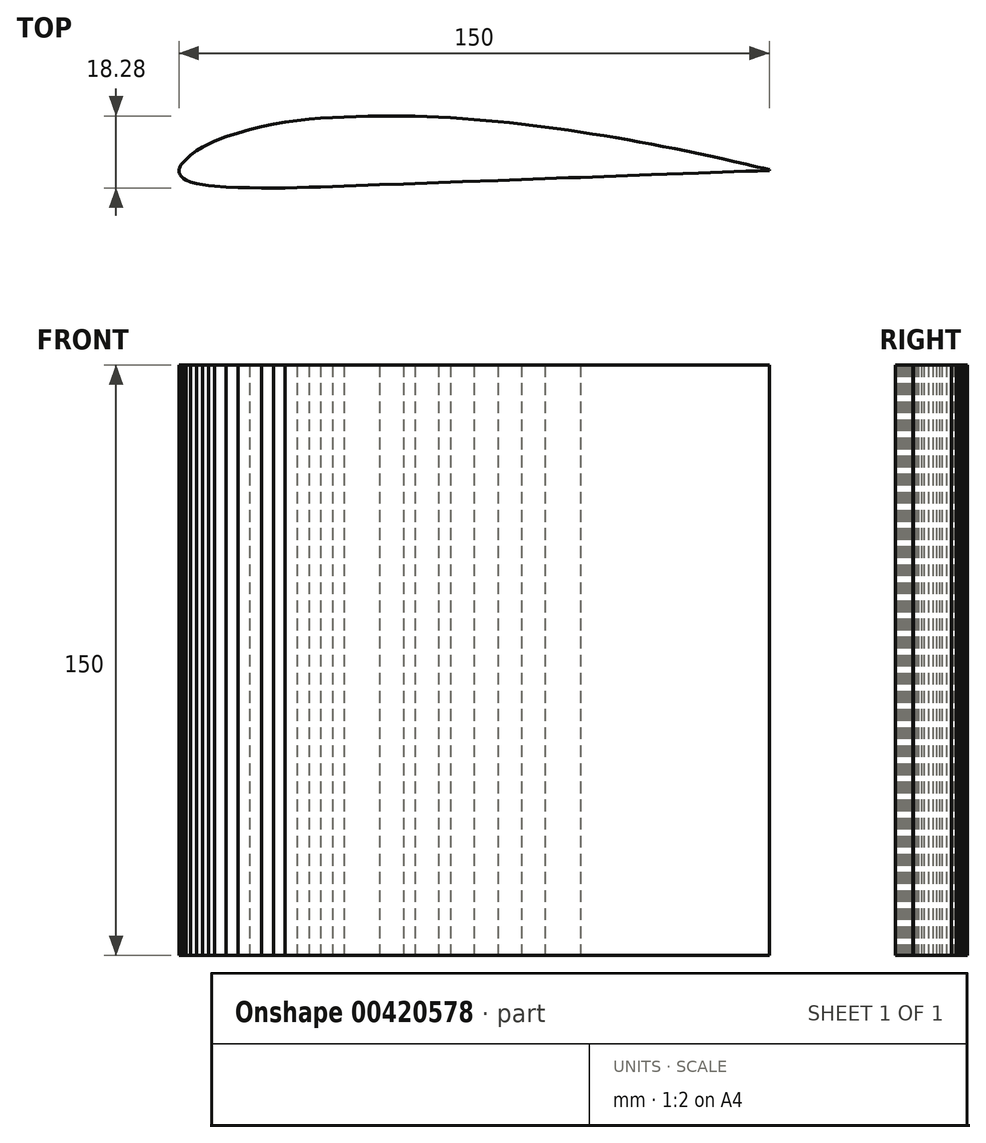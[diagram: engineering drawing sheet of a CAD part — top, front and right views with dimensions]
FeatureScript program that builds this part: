
annotation { "Feature Type Name" : "Feature", "Feature Type Description" : "" }
export const myFeature = defineFeature(function(context is Context, id is Id, definition is map)
    precondition{}
    {
        {
            var Q0;
            Q0=qCreatedBy(makeId("Top.planeOp"),FACE);
            var sketch = newSketch(context, id + "F0", { "sketchPlane" : qUnion([Q0])});
            skLineSegment(sketch, "E0", {"start": v(75, -1.06) * mm, "end": v(73.5, -0.7) * mm});
            skLineSegment(sketch, "E1", {"start": v(73.5, -0.7) * mm, "end": v(72, -0.35) * mm});
            skLineSegment(sketch, "E2", {"start": v(72, -0.35) * mm, "end": v(70.5, 0) * mm});
            skLineSegment(sketch, "E3", {"start": v(70.5, 0) * mm, "end": v(69, 0.35) * mm});
            skLineSegment(sketch, "E4", {"start": v(69, 0.35) * mm, "end": v(66, 1.04) * mm});
            skLineSegment(sketch, "E5", {"start": v(66, 1.04) * mm, "end": v(63, 1.72) * mm});
            skLineSegment(sketch, "E6", {"start": v(63, 1.72) * mm, "end": v(60, 2.38) * mm});
            skLineSegment(sketch, "E7", {"start": v(60, 2.38) * mm, "end": v(57, 3.02) * mm});
            skLineSegment(sketch, "E8", {"start": v(57, 3.02) * mm, "end": v(54, 3.65) * mm});
            skLineSegment(sketch, "E9", {"start": v(54, 3.65) * mm, "end": v(51, 4.26) * mm});
            skLineSegment(sketch, "E10", {"start": v(51, 4.26) * mm, "end": v(48, 4.85) * mm});
            skLineSegment(sketch, "E11", {"start": v(48, 4.85) * mm, "end": v(45, 5.43) * mm});
            skLineSegment(sketch, "E12", {"start": v(45, 5.43) * mm, "end": v(42, 5.99) * mm});
            skLineSegment(sketch, "E13", {"start": v(42, 5.99) * mm, "end": v(39, 6.54) * mm});
            skLineSegment(sketch, "E14", {"start": v(39, 6.54) * mm, "end": v(36, 7.07) * mm});
            skLineSegment(sketch, "E15", {"start": v(36, 7.07) * mm, "end": v(33, 7.57) * mm});
            skLineSegment(sketch, "E16", {"start": v(33, 7.57) * mm, "end": v(30, 8.06) * mm});
            skLineSegment(sketch, "E17", {"start": v(30, 8.06) * mm, "end": v(27, 8.54) * mm});
            skLineSegment(sketch, "E18", {"start": v(27, 8.54) * mm, "end": v(24, 8.99) * mm});
            skLineSegment(sketch, "E19", {"start": v(24, 8.99) * mm, "end": v(21, 9.42) * mm});
            skLineSegment(sketch, "E20", {"start": v(21, 9.42) * mm, "end": v(18, 9.83) * mm});
            skLineSegment(sketch, "E21", {"start": v(18, 9.83) * mm, "end": v(15, 10.2) * mm});
            skLineSegment(sketch, "E22", {"start": v(15, 10.2) * mm, "end": v(12, 10.57) * mm});
            skLineSegment(sketch, "E23", {"start": v(12, 10.57) * mm, "end": v(9, 10.9) * mm});
            skLineSegment(sketch, "E24", {"start": v(9, 10.9) * mm, "end": v(6, 11.2) * mm});
            skLineSegment(sketch, "E25", {"start": v(6, 11.2) * mm, "end": v(3, 11.48) * mm});
            skLineSegment(sketch, "E26", {"start": v(3, 11.48) * mm, "end": v(0, 11.73) * mm});
            skLineSegment(sketch, "E27", {"start": v(0, 11.73) * mm, "end": v(-3, 11.95) * mm});
            skLineSegment(sketch, "E28", {"start": v(-3, 11.95) * mm, "end": v(-6, 12.15) * mm});
            skLineSegment(sketch, "E29", {"start": v(-6, 12.15) * mm, "end": v(-9, 12.3) * mm});
            skLineSegment(sketch, "E30", {"start": v(-9, 12.3) * mm, "end": v(-12, 12.43) * mm});
            skLineSegment(sketch, "E31", {"start": v(-12, 12.43) * mm, "end": v(-15, 12.53) * mm});
            skLineSegment(sketch, "E32", {"start": v(-15, 12.53) * mm, "end": v(-18, 12.58) * mm});
            skLineSegment(sketch, "E33", {"start": v(-18, 12.58) * mm, "end": v(-21, 12.59) * mm});
            skLineSegment(sketch, "E34", {"start": v(-21, 12.59) * mm, "end": v(-24, 12.58) * mm});
            skLineSegment(sketch, "E35", {"start": v(-24, 12.58) * mm, "end": v(-27, 12.53) * mm});
            skLineSegment(sketch, "E36", {"start": v(-27, 12.53) * mm, "end": v(-30, 12.45) * mm});
            skLineSegment(sketch, "E37", {"start": v(-30, 12.45) * mm, "end": v(-33, 12.35) * mm});
            skLineSegment(sketch, "E38", {"start": v(-33, 12.35) * mm, "end": v(-36, 12.2) * mm});
            skLineSegment(sketch, "E39", {"start": v(-36, 12.2) * mm, "end": v(-39, 12.02) * mm});
            skLineSegment(sketch, "E40", {"start": v(-39, 12.02) * mm, "end": v(-42, 11.77) * mm});
            skLineSegment(sketch, "E41", {"start": v(-42, 11.77) * mm, "end": v(-45, 11.44) * mm});
            skLineSegment(sketch, "E42", {"start": v(-45, 11.44) * mm, "end": v(-48, 11.01) * mm});
            skLineSegment(sketch, "E43", {"start": v(-48, 11.01) * mm, "end": v(-51, 10.49) * mm});
            skLineSegment(sketch, "E44", {"start": v(-51, 10.49) * mm, "end": v(-54, 9.87) * mm});
            skLineSegment(sketch, "E45", {"start": v(-54, 9.87) * mm, "end": v(-57, 9.14) * mm});
            skLineSegment(sketch, "E46", {"start": v(-57, 9.14) * mm, "end": v(-60, 8.3) * mm});
            skLineSegment(sketch, "E47", {"start": v(-60, 8.3) * mm, "end": v(-63, 7.31) * mm});
            skLineSegment(sketch, "E48", {"start": v(-63, 7.31) * mm, "end": v(-66, 6.16) * mm});
            skLineSegment(sketch, "E49", {"start": v(-66, 6.16) * mm, "end": v(-67.5, 5.49) * mm});
            skLineSegment(sketch, "E50", {"start": v(-67.5, 5.49) * mm, "end": v(-69, 4.72) * mm});
            skLineSegment(sketch, "E51", {"start": v(-69, 4.72) * mm, "end": v(-70.5, 3.8) * mm});
            skLineSegment(sketch, "E52", {"start": v(-70.5, 3.8) * mm, "end": v(-72, 2.66) * mm});
            skLineSegment(sketch, "E53", {"start": v(-72, 2.66) * mm, "end": v(-73.2, 1.53) * mm});
            skLineSegment(sketch, "E54", {"start": v(-73.2, 1.53) * mm, "end": v(-73.8, 0.91) * mm});
            skLineSegment(sketch, "E55", {"start": v(-73.8, 0.91) * mm, "end": v(-74.4, 0.19) * mm});
            skLineSegment(sketch, "E56", {"start": v(-74.4, 0.19) * mm, "end": v(-74.7, -0.28) * mm});
            skLineSegment(sketch, "E57", {"start": v(-74.7, -0.28) * mm, "end": v(-74.85, -0.6) * mm});
            skLineSegment(sketch, "E58", {"start": v(-74.85, -0.6) * mm, "end": v(-74.92, -0.8) * mm});
            skLineSegment(sketch, "E59", {"start": v(-74.92, -0.8) * mm, "end": v(-75, -1.15) * mm});
            skLineSegment(sketch, "E60", {"start": v(-75, -1.15) * mm, "end": v(-74.92, -1.85) * mm});
            skLineSegment(sketch, "E61", {"start": v(-74.92, -1.85) * mm, "end": v(-74.85, -2.04) * mm});
            skLineSegment(sketch, "E62", {"start": v(-74.85, -2.04) * mm, "end": v(-74.7, -2.32) * mm});
            skLineSegment(sketch, "E63", {"start": v(-74.7, -2.32) * mm, "end": v(-74.4, -2.73) * mm});
            skLineSegment(sketch, "E64", {"start": v(-74.4, -2.73) * mm, "end": v(-73.8, -3.29) * mm});
            skLineSegment(sketch, "E65", {"start": v(-73.8, -3.29) * mm, "end": v(-73.2, -3.7) * mm});
            skLineSegment(sketch, "E66", {"start": v(-73.2, -3.7) * mm, "end": v(-72, -4.19) * mm});
            skLineSegment(sketch, "E67", {"start": v(-72, -4.19) * mm, "end": v(-70.5, -4.54) * mm});
            skLineSegment(sketch, "E68", {"start": v(-70.5, -4.54) * mm, "end": v(-69, -4.83) * mm});
            skLineSegment(sketch, "E69", {"start": v(-69, -4.83) * mm, "end": v(-67.5, -5.06) * mm});
            skLineSegment(sketch, "E70", {"start": v(-67.5, -5.06) * mm, "end": v(-66, -5.22) * mm});
            skLineSegment(sketch, "E71", {"start": v(-66, -5.22) * mm, "end": v(-63, -5.42) * mm});
            skLineSegment(sketch, "E72", {"start": v(-63, -5.42) * mm, "end": v(-60, -5.56) * mm});
            skLineSegment(sketch, "E73", {"start": v(-60, -5.56) * mm, "end": v(-57, -5.64) * mm});
            skLineSegment(sketch, "E74", {"start": v(-57, -5.64) * mm, "end": v(-54, -5.7) * mm});
            skLineSegment(sketch, "E75", {"start": v(-54, -5.7) * mm, "end": v(-51, -5.7) * mm});
            skLineSegment(sketch, "E76", {"start": v(-51, -5.7) * mm, "end": v(-48, -5.66) * mm});
            skLineSegment(sketch, "E77", {"start": v(-48, -5.66) * mm, "end": v(-45, -5.6) * mm});
            skLineSegment(sketch, "E78", {"start": v(-45, -5.6) * mm, "end": v(-42, -5.52) * mm});
            skLineSegment(sketch, "E79", {"start": v(-42, -5.52) * mm, "end": v(-39, -5.43) * mm});
            skLineSegment(sketch, "E80", {"start": v(-39, -5.43) * mm, "end": v(-30, -5.1) * mm});
            skLineSegment(sketch, "E81", {"start": v(-30, -5.1) * mm, "end": v(-27, -4.98) * mm});
            skLineSegment(sketch, "E82", {"start": v(-27, -4.98) * mm, "end": v(-24, -4.87) * mm});
            skLineSegment(sketch, "E83", {"start": v(-24, -4.87) * mm, "end": v(-18, -4.65) * mm});
            skLineSegment(sketch, "E84", {"start": v(-18, -4.65) * mm, "end": v(-15, -4.55) * mm});
            skLineSegment(sketch, "E85", {"start": v(-15, -4.55) * mm, "end": v(-12, -4.44) * mm});
            skLineSegment(sketch, "E86", {"start": v(-12, -4.44) * mm, "end": v(-6, -4.22) * mm});
            skLineSegment(sketch, "E87", {"start": v(-6, -4.22) * mm, "end": v(-3, -4.1) * mm});
            skLineSegment(sketch, "E88", {"start": v(-3, -4.1) * mm, "end": v(6, -3.77) * mm});
            skLineSegment(sketch, "E89", {"start": v(6, -3.77) * mm, "end": v(9, -3.66) * mm});
            skLineSegment(sketch, "E90", {"start": v(9, -3.66) * mm, "end": v(24, -3.11) * mm});
            skLineSegment(sketch, "E91", {"start": v(24, -3.11) * mm, "end": v(27, -3) * mm});
            skLineSegment(sketch, "E92", {"start": v(27, -3) * mm, "end": v(42, -2.45) * mm});
            skLineSegment(sketch, "E93", {"start": v(42, -2.45) * mm, "end": v(45, -2.34) * mm});
            skLineSegment(sketch, "E94", {"start": v(45, -2.34) * mm, "end": v(57, -1.9) * mm});
            skLineSegment(sketch, "E95", {"start": v(57, -1.9) * mm, "end": v(60, -1.8) * mm});
            skLineSegment(sketch, "E96", {"start": v(60, -1.8) * mm, "end": v(69, -1.46) * mm});
            skLineSegment(sketch, "E97", {"start": v(69, -1.46) * mm, "end": v(70.5, -1.41) * mm});
            skLineSegment(sketch, "E98", {"start": v(70.5, -1.41) * mm, "end": v(72, -1.35) * mm});
            skLineSegment(sketch, "E99", {"start": v(72, -1.35) * mm, "end": v(73.5, -1.3) * mm});
            skLineSegment(sketch, "E100", {"start": v(73.5, -1.3) * mm, "end": v(75, -1.24) * mm});
            skLineSegment(sketch, "E101", {"start": v(75, -1.06) * mm, "end": v(75, -1.24) * mm});
            skSolve(sketch);
        }
        {
            var Q0;
            Q0=makeQuery(id+"F0.imprint","IMPRINT",FACE,{"disambiguationData":[TD([[makeQuery(id+"F0.imprint","IMPRINT",EDGE,{"derivedFrom":sQuery(id+"F0.wireOp",EDGE,"E0")}),1.0]])]});
            var Q1;
            Q1=sQuery(id+"F0.wireOp",EDGE,"E83");
            var Q2;
            Q2=sQuery(id+"F0.wireOp",EDGE,"E96");
            var Q3;
            Q3=sQuery(id+"F0.wireOp",EDGE,"E90");
            var Q4;
            Q4=sQuery(id+"F0.wireOp",EDGE,"E88");
            var Q5;
            Q5=sQuery(id+"F0.wireOp",EDGE,"E80");
            var Q6;
            Q6=sQuery(id+"F0.wireOp",EDGE,"E86");
            var Q7;
            Q7=sQuery(id+"F0.wireOp",EDGE,"E94");
            var Q8;
            Q8=sQuery(id+"F0.wireOp",EDGE,"E92");
            var Q9;
            Q9=sQuery(id+"F0.wireOp",EDGE,"E22");
            var Q10;
            Q10=sQuery(id+"F0.wireOp",EDGE,"E25");
            var Q11;
            Q11=sQuery(id+"F0.wireOp",EDGE,"E89");
            var Q12;
            Q12=sQuery(id+"F0.wireOp",EDGE,"E67");
            var Q13;
            Q13=sQuery(id+"F0.wireOp",EDGE,"E5");
            var Q14;
            Q14=sQuery(id+"F0.wireOp",EDGE,"E70");
            var Q15;
            Q15=sQuery(id+"F0.wireOp",EDGE,"E24");
            var Q16;
            Q16=sQuery(id+"F0.wireOp",EDGE,"E39");
            var Q17;
            Q17=sQuery(id+"F0.wireOp",EDGE,"E87");
            var Q18;
            Q18=sQuery(id+"F0.wireOp",EDGE,"E31");
            var Q19;
            Q19=sQuery(id+"F0.wireOp",EDGE,"E38");
            var Q20;
            Q20=sQuery(id+"F0.wireOp",EDGE,"E1");
            var Q21;
            Q21=sQuery(id+"F0.wireOp",EDGE,"E34");
            var Q22;
            Q22=sQuery(id+"F0.wireOp",EDGE,"E11");
            var Q23;
            Q23=sQuery(id+"F0.wireOp",EDGE,"E23");
            var Q24;
            Q24=sQuery(id+"F0.wireOp",EDGE,"E72");
            var Q25;
            Q25=sQuery(id+"F0.wireOp",EDGE,"E81");
            var Q26;
            Q26=sQuery(id+"F0.wireOp",EDGE,"E49");
            var Q27;
            Q27=sQuery(id+"F0.wireOp",EDGE,"E33");
            var Q28;
            Q28=sQuery(id+"F0.wireOp",EDGE,"E41");
            var Q29;
            Q29=sQuery(id+"F0.wireOp",EDGE,"E46");
            var Q30;
            Q30=sQuery(id+"F0.wireOp",EDGE,"E19");
            var Q31;
            Q31=sQuery(id+"F0.wireOp",EDGE,"E29");
            var Q32;
            Q32=sQuery(id+"F0.wireOp",EDGE,"E45");
            var Q33;
            Q33=sQuery(id+"F0.wireOp",EDGE,"E77");
            var Q34;
            Q34=sQuery(id+"F0.wireOp",EDGE,"E42");
            var Q35;
            Q35=sQuery(id+"F0.wireOp",EDGE,"E91");
            var Q36;
            Q36=sQuery(id+"F0.wireOp",EDGE,"E75");
            var Q37;
            Q37=sQuery(id+"F0.wireOp",EDGE,"E27");
            var Q38;
            Q38=sQuery(id+"F0.wireOp",EDGE,"E43");
            var Q39;
            Q39=sQuery(id+"F0.wireOp",EDGE,"E35");
            var Q40;
            Q40=sQuery(id+"F0.wireOp",EDGE,"E51");
            var Q41;
            Q41=sQuery(id+"F0.wireOp",EDGE,"E74");
            var Q42;
            Q42=sQuery(id+"F0.wireOp",EDGE,"E26");
            var Q43;
            Q43=sQuery(id+"F0.wireOp",EDGE,"E82");
            var Q44;
            Q44=sQuery(id+"F0.wireOp",EDGE,"E18");
            var Q45;
            Q45=sQuery(id+"F0.wireOp",EDGE,"E73");
            var Q46;
            Q46=sQuery(id+"F0.wireOp",EDGE,"E17");
            var Q47;
            Q47=sQuery(id+"F0.wireOp",EDGE,"E40");
            var Q48;
            Q48=sQuery(id+"F0.wireOp",EDGE,"E48");
            var Q49;
            Q49=sQuery(id+"F0.wireOp",EDGE,"E32");
            var Q50;
            Q50=sQuery(id+"F0.wireOp",EDGE,"E16");
            var Q51;
            Q51=sQuery(id+"F0.wireOp",EDGE,"E71");
            var Q52;
            Q52=sQuery(id+"F0.wireOp",EDGE,"E12");
            var Q53;
            Q53=sQuery(id+"F0.wireOp",EDGE,"E10");
            var Q54;
            Q54=sQuery(id+"F0.wireOp",EDGE,"E9");
            var Q55;
            Q55=sQuery(id+"F0.wireOp",EDGE,"E8");
            var Q56;
            Q56=sQuery(id+"F0.wireOp",EDGE,"E7");
            var Q57;
            Q57=sQuery(id+"F0.wireOp",EDGE,"E6");
            var Q58;
            Q58=sQuery(id+"F0.wireOp",EDGE,"E4");
            var Q59;
            Q59=sQuery(id+"F0.wireOp",EDGE,"E2");
            var Q60;
            Q60=sQuery(id+"F0.wireOp",EDGE,"E15");
            var Q61;
            Q61=sQuery(id+"F0.wireOp",EDGE,"E14");
            var Q62;
            Q62=sQuery(id+"F0.wireOp",EDGE,"E13");
            var Q63;
            Q63=sQuery(id+"F0.wireOp",EDGE,"E95");
            var Q64;
            Q64=sQuery(id+"F0.wireOp",EDGE,"E98");
            var Q65;
            Q65=sQuery(id+"F0.wireOp",EDGE,"E54");
            var Q66;
            Q66=sQuery(id+"F0.wireOp",EDGE,"E47");
            var Q67;
            Q67=sQuery(id+"F0.wireOp",EDGE,"E79");
            var Q68;
            Q68=sQuery(id+"F0.wireOp",EDGE,"E37");
            var Q69;
            Q69=sQuery(id+"F0.wireOp",EDGE,"E30");
            var Q70;
            Q70=sQuery(id+"F0.wireOp",EDGE,"E53");
            var Q71;
            Q71=sQuery(id+"F0.wireOp",EDGE,"E69");
            var Q72;
            Q72=sQuery(id+"F0.wireOp",EDGE,"E85");
            var Q73;
            Q73=sQuery(id+"F0.wireOp",EDGE,"E21");
            var Q74;
            Q74=sQuery(id+"F0.wireOp",EDGE,"E76");
            var Q75;
            Q75=sQuery(id+"F0.wireOp",EDGE,"E78");
            var Q76;
            Q76=sQuery(id+"F0.wireOp",EDGE,"E28");
            var Q77;
            Q77=sQuery(id+"F0.wireOp",EDGE,"E44");
            var Q78;
            Q78=sQuery(id+"F0.wireOp",EDGE,"E100");
            var Q79;
            Q79=sQuery(id+"F0.wireOp",EDGE,"E93");
            var Q80;
            Q80=sQuery(id+"F0.wireOp",EDGE,"E36");
            var Q81;
            Q81=sQuery(id+"F0.wireOp",EDGE,"E52");
            var Q82;
            Q82=sQuery(id+"F0.wireOp",EDGE,"E50");
            var Q83;
            Q83=sQuery(id+"F0.wireOp",EDGE,"E66");
            var Q84;
            Q84=sQuery(id+"F0.wireOp",EDGE,"E84");
            var Q85;
            Q85=sQuery(id+"F0.wireOp",EDGE,"E68");
            var Q86;
            Q86=sQuery(id+"F0.wireOp",EDGE,"E20");
            var Q87;
            Q87=sQuery(id+"F0.wireOp",EDGE,"E65");
            var Q88;
            Q88=sQuery(id+"F0.wireOp",EDGE,"E0");
            var Q89;
            Q89=sQuery(id+"F0.wireOp",EDGE,"E99");
            var Q90;
            Q90=sQuery(id+"F0.wireOp",EDGE,"E97");
            var Q91;
            Q91=sQuery(id+"F0.wireOp",EDGE,"E3");
            var Q92;
            Q92=sQuery(id+"F0.wireOp",EDGE,"E101");
            var Q93;
            Q93=sQuery(id+"F0.wireOp",EDGE,"E55");
            var Q94;
            Q94=sQuery(id+"F0.wireOp",EDGE,"E57");
            var Q95;
            Q95=sQuery(id+"F0.wireOp",EDGE,"E64");
            var Q96;
            Q96=sQuery(id+"F0.wireOp",EDGE,"E56");
            var Q97;
            Q97=sQuery(id+"F0.wireOp",EDGE,"E62");
            var Q98;
            Q98=sQuery(id+"F0.wireOp",EDGE,"E60");
            var Q99;
            Q99=sQuery(id+"F0.wireOp",EDGE,"E63");
            var Q100;
            Q100=sQuery(id+"F0.wireOp",EDGE,"E59");
            var Q101;
            Q101=sQuery(id+"F0.wireOp",EDGE,"E61");
            var Q102;
            Q102=sQuery(id+"F0.wireOp",EDGE,"E58");
            extrude(context, id + "F1", {"entities" : qUnion([Q0]), "surfaceEntities" : qUnion([Q1, Q2, Q3, Q4, Q5, Q6, Q7, Q8, Q9, Q10, Q11, Q12, Q13, Q14, Q15, Q16, Q17, Q18, Q19, Q20, Q21, Q22, Q23, Q24, Q25, Q26, Q27, Q28, Q29, Q30, Q31, Q32, Q33, Q34, Q35, Q36, Q37, Q38, Q39, Q40, Q41, Q42, Q43, Q44, Q45, Q46, Q47, Q48, Q49, Q50, Q51, Q52, Q53, Q54, Q55, Q56, Q57, Q58, Q59, Q60, Q61, Q62, Q63, Q64, Q65, Q66, Q67, Q68, Q69, Q70, Q71, Q72, Q73, Q74, Q75, Q76, Q77, Q78, Q79, Q80, Q81, Q82, Q83, Q84, Q85, Q86, Q87, Q88, Q89, Q90, Q91, Q92, Q93, Q94, Q95, Q96, Q97, Q98, Q99, Q100, Q101, Q102]), "depth" : 150 * mm});
        }
    });
